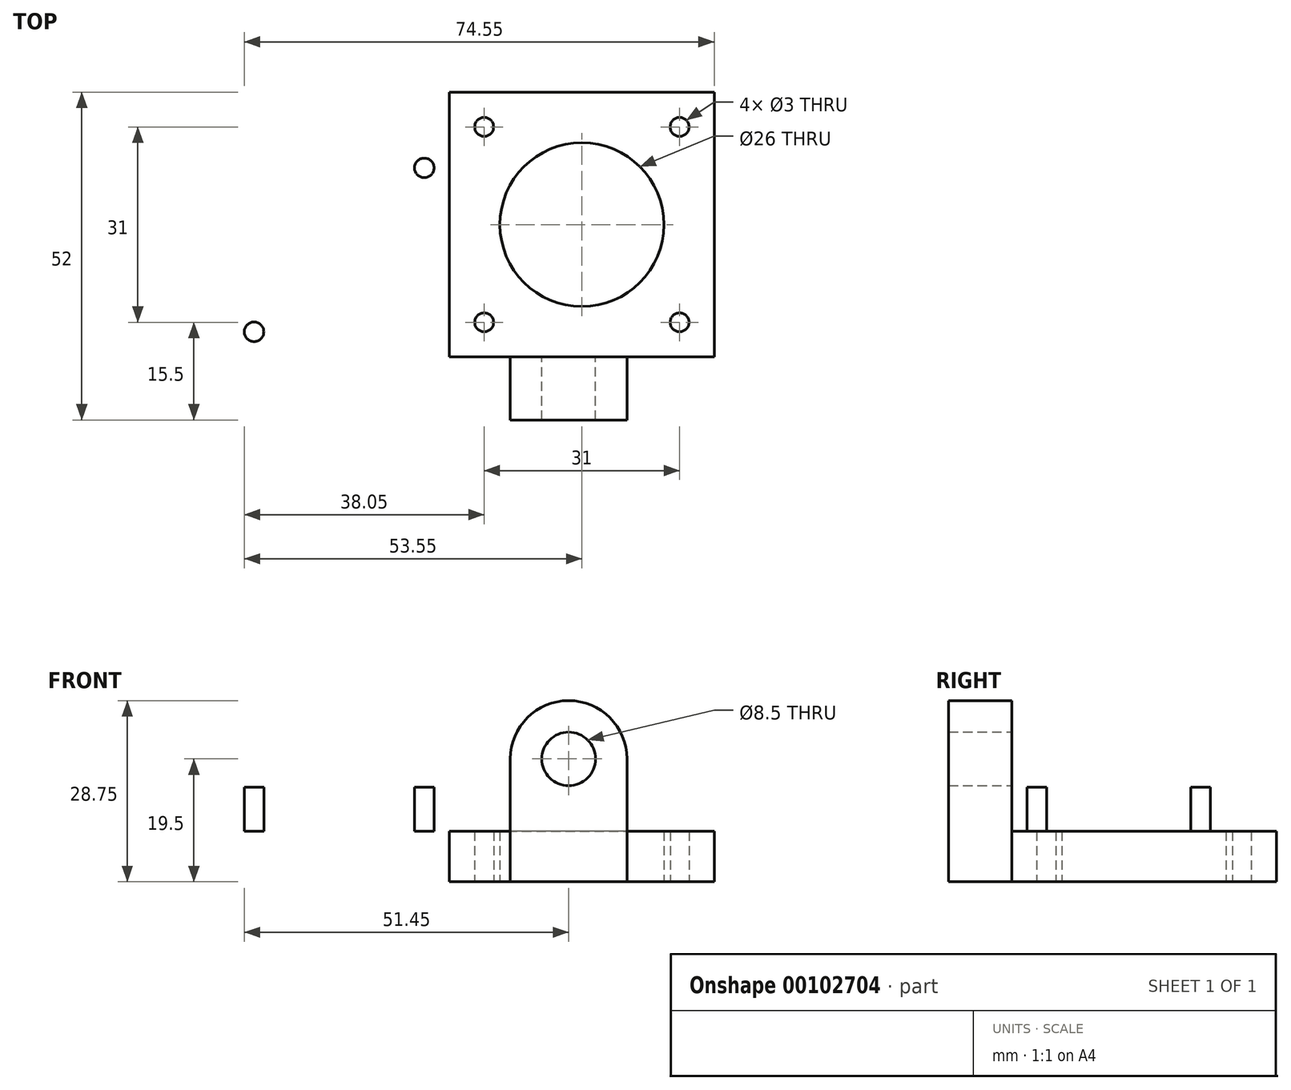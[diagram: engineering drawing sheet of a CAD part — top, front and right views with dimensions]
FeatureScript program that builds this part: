
annotation { "Feature Type Name" : "Feature", "Feature Type Description" : "" }
export const myFeature = defineFeature(function(context is Context, id is Id, definition is map)
    precondition{}
    {
        {
            var Q0;
            Q0=qCreatedBy(makeId("Top.planeOp"),FACE);
            var sketch = newSketch(context, id + "F0", { "sketchPlane" : qUnion([Q0])});
            skLineSegment(sketch, "E0.top", {"start": v(-21, 21) * mm, "end": v(21, 21) * mm});
            skLineSegment(sketch, "E0.left", {"start": v(-21, -21) * mm, "end": v(-21, 21) * mm});
            skPoint(sketch, "E1", {"position": v(0, -21) * mm});
            skCircle(sketch, "E2", {"center": v(-15.5, -15.5) * mm, "radius": 1.5 * mm});
            skCircle(sketch, "E3.MirrorC", {"center": v(15.5, -15.5) * mm, "radius": 1.5 * mm});
            skCircle(sketch, "E4.MirrorC", {"center": v(-15.5, 15.5) * mm, "radius": 1.5 * mm});
            skCircle(sketch, "E5.MirrorC", {"center": v(15.5, 15.5) * mm, "radius": 1.5 * mm});
            skLineSegment(sketch, "E6", {"start": v(-16, -21) * mm, "end": v(-21, -16) * mm, "construction": true});
            skLineSegment(sketch, "E7.MirrorCS", {"start": v(16, -21) * mm, "end": v(21, -16) * mm, "construction": true});
            skLineSegment(sketch, "E8.MirrorCS", {"start": v(-16, 21) * mm, "end": v(-21, 16) * mm, "construction": true});
            skLineSegment(sketch, "E9.MirrorCS", {"start": v(16, 21) * mm, "end": v(21, 16) * mm, "construction": true});
            skCircle(sketch, "E10", {"center": v(0, 0) * mm, "radius": 11 * mm, "construction": true});
            skLineSegment(sketch, "E11", {"start": v(-4, -21) * mm, "end": v(-4, -47.52) * mm, "construction": true});
            skLineSegment(sketch, "E12.MirrorCS", {"start": v(4, -21) * mm, "end": v(4, -47.52) * mm, "construction": true});
            skLineSegment(sketch, "E13", {"start": v(0, -21) * mm, "end": v(21, -21) * mm});
            skCircle(sketch, "E14", {"center": v(0, 0) * mm, "radius": 13 * mm});
            skLineSegment(sketch, "E15", {"start": v(21, -16) * mm, "end": v(21, 21) * mm});
            skLineSegment(sketch, "E16", {"start": v(0, -21) * mm, "end": v(-21, -21) * mm});
            skLineSegment(sketch, "E17", {"start": v(21, -21) * mm, "end": v(21, -16) * mm});
            skPoint(sketch, "E18", {"position": v(-21, 0) * mm});
            skLineSegment(sketch, "E19", {"start": v(-22, -21) * mm, "end": v(-22, 21) * mm, "construction": true});
            skLineSegment(sketch, "E20", {"start": v(-21, -21) * mm, "end": v(-56, -21) * mm});
            skLineSegment(sketch, "E21", {"start": v(-56, -21) * mm, "end": v(-56, 13) * mm});
            skLineSegment(sketch, "E22", {"start": v(-56, 13) * mm, "end": v(-21, 13) * mm});
            skLineSegment(sketch, "E23", {"start": v(-38.5, 13) * mm, "end": v(-38.5, -21) * mm, "construction": true});
            skLineSegment(sketch, "E24", {"start": v(-56, -4) * mm, "end": v(-21, -4) * mm, "construction": true});
            skCircle(sketch, "E25", {"center": v(-52, 9) * mm, "radius": 1.55 * mm});
            skCircle(sketch, "E26.MirrorC", {"center": v(-25, 9) * mm, "radius": 1.55 * mm});
            skCircle(sketch, "E27.MirrorC", {"center": v(-52, -17) * mm, "radius": 1.55 * mm});
            skCircle(sketch, "E28.MirrorC", {"center": v(-25, -17) * mm, "radius": 1.55 * mm});
            skSolve(sketch);
        }
        {
            var Q0;
            Q0 = qSketchRegion(id + "F0", true);
            extrude(context, id + "F1", {"entities" : qUnion([Q0]), "depth" : 8 * mm});
        }
        {
            var Q0;
            Q0=makeQuery(id+"F1.opExtrude","SWEPT_FACE",FACE,{"disambiguationData":[OSD([sQuery(id+"F0.wireOp",EDGE,"E13"),sQuery(id+"F0.wireOp",EDGE,"E16")])]});
            var sketch = newSketch(context, id + "F2", { "sketchPlane" : qUnion([Q0])});
            skCircle(sketch, "E29", {"center": v(-2.1, 19.5) * mm, "radius": 4.25 * mm});
            skLineSegment(sketch, "E30.0", {"start": v(-13, 8) * mm, "end": v(13, 8) * mm});
            skPoint(sketch, "E31", {"position": v(0, 8) * mm});
            skLineSegment(sketch, "E32", {"start": v(-11.35, 19.5) * mm, "end": v(-11.35, 0) * mm});
            skLineSegment(sketch, "E33.MirrorCS", {"start": v(7.15, 19.5) * mm, "end": v(7.15, 0) * mm});
            skArc(sketch, "E34", {"start": v(7.15, 19.5) * mm, "mid": v(-2.1, 28.75) * mm, "end": v(-11.35, 19.5) * mm});
            skLineSegment(sketch, "E35", {"start": v(-2.1, 19.5) * mm, "end": v(-2.1, -7.76) * mm, "construction": true});
            skSolve(sketch);
        }
        {
            var Q0;
            {var subQ0=sQuery(id+"F2.wireOp",EDGE,"E33.MirrorCS");var subQ1=sQuery(id+"F2.wireOp",EDGE,"E30.0");var subQ2=makeQuery(id+"F2.imprint","INTERSECT",VERTEX,{"derivedFrom":[subQ1,subQ0]});Q0=makeQuery(id+"F2.imprint","IMPRINT",FACE,{"disambiguationData":[TD([[makeQuery(id+"F2.imprint","IMPRINT",EDGE,{"disambiguationData":[TD([[subQ2,-1.0]])],"derivedFrom":subQ1}),1.0]])]});}
            var Q1;
            Q1=makeQuery(id+"F2.imprint","IMPRINT",FACE,{"disambiguationData":[TD([[makeQuery(id+"F2.imprint","IMPRINT",EDGE,{"derivedFrom":sQuery(id+"F2.wireOp",EDGE,"E29")}),-1.0]])]});
            var Q2;
            Q2=makeQuery(id+"F1.opExtrude","SWEPT_FACE",FACE,{"disambiguationData":[OSD([sQuery(id+"F0.wireOp",EDGE,"E16")])]});
            extrude(context, id + "F3", {"entities" : qUnion([Q0, Q1]), "operationType" : NewBodyOperationType.ADD, "endBoundEntityFace" : qUnion([Q2]), "depth" : 10 * mm});
        }
        {
            var Q0;
            {var subQ0=sQuery(id+"F0.wireOp",EDGE,"E21");var subQ6=sQuery(id+"F0.wireOp",EDGE,"E20");var subQ8=sQuery(id+"F0.wireOp",EDGE,"E16");var subQ11=sQuery(id+"F0.wireOp",EDGE,"E13");Q0=makeQuery(id+"F3.boolean.opBoolean","SPLIT",FACE,{"disambiguationData":[TD([makeQuery(id+"F1.opExtrude","SWEPT_FACE",FACE,{"disambiguationData":[OSD([subQ0])]})])],"derivedFrom":makeQuery(id+"F1.opExtrude","SWEPT_FACE",FACE,{"disambiguationData":[OSD([subQ11,subQ8,subQ6])]})});}
            var sketch = newSketch(context, id + "F4", { "sketchPlane" : qUnion([Q0])});
            skLineSegment(sketch, "E36", {"start": v(-56, 8) * mm, "end": v(-56, 15) * mm});
            skPoint(sketch, "E37.0", {"position": v(-22, 0) * mm});
            skLineSegment(sketch, "E38", {"start": v(-22, 0) * mm, "end": v(-22, 15) * mm});
            skLineSegment(sketch, "E39", {"start": v(-22, 15) * mm, "end": v(-56, 15) * mm});
            skArc(sketch, "E40", {"start": v(-49.25, 15) * mm, "mid": v(-39, 4.75) * mm, "end": v(-28.75, 15) * mm});
            skLineSegment(sketch, "E41.0", {"start": v(-56, 8) * mm, "end": v(-56, 0) * mm});
            skLineSegment(sketch, "E42.0", {"start": v(-21, 0) * mm, "end": v(-56, 0) * mm});
            skSolve(sketch);
        }
        {
            var Q0;
            {var subQ0=sQuery(id+"F4.wireOp",EDGE,"E36");Q0=makeQuery(id+"F4.imprint","IMPRINT",FACE,{"disambiguationData":[TD([[makeQuery(id+"F4.imprint","IMPRINT",EDGE,{"derivedFrom":subQ0}),-1.0]])]});}
            var Q1;
            {var subQ0=sQuery(id+"F4.wireOp",EDGE,"E39");var subQ1=sQuery(id+"F4.wireOp",EDGE,"E38");var subQ2=makeQuery(id+"F4.imprint","INTERSECT",VERTEX,{"derivedFrom":[subQ1,subQ0]});Q1=makeQuery(id+"F4.imprint","IMPRINT",FACE,{"disambiguationData":[TD([[makeQuery(id+"F4.imprint","IMPRINT",EDGE,{"disambiguationData":[TD([[subQ2,-1.0]])],"derivedFrom":subQ0}),1.0]])]});}
            var Q2;
            Q2=makeQuery(id+"F1.opExtrude","SWEPT_FACE",FACE,{"disambiguationData":[OSD([sQuery(id+"F0.wireOp",EDGE,"E22")])]});
            extrude(context, id + "F5", {"entities" : qUnion([Q0, Q1]), "operationType" : NewBodyOperationType.ADD, "endBound" : BoundingType.UP_TO_SURFACE, "oppositeDirection" : true, "endBoundEntityFace" : qUnion([Q2]), "depth" : 25 * mm});
        }
        {
            var Q0;
            {var subQ0=sQuery(id+"F4.wireOp",EDGE,"E40");var subQ1=sQuery(id+"F2.wireOp",EDGE,"E32");var subQ2=sQuery(id+"F0.wireOp",EDGE,"E20");var subQ3=sQuery(id+"F0.wireOp",EDGE,"E16");var subQ4=sQuery(id+"F0.wireOp",EDGE,"E13");var subQ5=sQuery(id+"F0.wireOp",EDGE,"E21");var subQ6=makeQuery(id+"F3.boolean.opBoolean","SPLIT",EDGE,{"disambiguationData":[TD([makeQuery(id+"F1.opExtrude","CAP_FACE",FACE,{"disambiguationData":[OSD([sQuery(id+"F0.wireOp",EDGE,"E0.top"),sQuery(id+"F0.wireOp",EDGE,"E0.left"),sQuery(id+"F0.wireOp",EDGE,"E2"),sQuery(id+"F0.wireOp",EDGE,"E3.MirrorC"),sQuery(id+"F0.wireOp",EDGE,"E4.MirrorC"),sQuery(id+"F0.wireOp",EDGE,"E5.MirrorC"),subQ4,sQuery(id+"F0.wireOp",EDGE,"E14"),sQuery(id+"F0.wireOp",EDGE,"E15"),subQ3,sQuery(id+"F0.wireOp",EDGE,"E17"),subQ2,subQ5,sQuery(id+"F0.wireOp",EDGE,"E22"),sQuery(id+"F0.wireOp",EDGE,"E25"),sQuery(id+"F0.wireOp",EDGE,"E26.MirrorC"),sQuery(id+"F0.wireOp",EDGE,"E27.MirrorC"),sQuery(id+"F0.wireOp",EDGE,"E28.MirrorC")])],"isStart":false}),makeQuery(id+"F1.opExtrude","SWEPT_FACE",FACE,{"disambiguationData":[OSD([subQ4,subQ3,subQ2])]}),makeQuery(id+"F1.opExtrude","SWEPT_FACE",FACE,{"disambiguationData":[OSD([subQ5])]}),makeQuery(id+"F3.opExtrude","CAP_FACE",FACE,{"disambiguationData":[OSD([subQ4,subQ3,subQ2,sQuery(id+"F2.wireOp",EDGE,"E29"),subQ1,sQuery(id+"F2.wireOp",EDGE,"E33.MirrorCS"),sQuery(id+"F2.wireOp",EDGE,"E34")])],"isStart":true}),makeQuery(id+"F3.opExtrude","SWEPT_FACE",FACE,{"disambiguationData":[OSD([subQ1])]})])],"derivedFrom":makeQuery(id+"F1.opExtrude","CAP_EDGE",EDGE,{"disambiguationData":[OSD([subQ4,subQ3,subQ2])],"isStart":false})});var subQ7=makeQuery(id+"F4.imprint","INTERSECT",VERTEX,{"disambiguationData":[OD(0.0)],"derivedFrom":[subQ6,subQ0]});Q0=makeQuery(id+"F4.imprint","IMPRINT",FACE,{"disambiguationData":[TD([[makeQuery(id+"F4.imprint","IMPRINT",EDGE,{"disambiguationData":[TD([[subQ7,-1.0]])],"derivedFrom":subQ0}),1.0]])]});}
            extrude(context, id + "F6", {"entities" : qUnion([Q0]), "operationType" : NewBodyOperationType.REMOVE, "endBound" : BoundingType.THROUGH_ALL, "oppositeDirection" : true, "depth" : 25 * mm});
        }
        {
            var Q0;
            Q0=makeQuery(id+"F0.imprint","IMPRINT",FACE,{"disambiguationData":[TD([[makeQuery(id+"F0.imprint","IMPRINT",EDGE,{"derivedFrom":sQuery(id+"F0.wireOp",EDGE,"E27.MirrorC")}),-1.0]])]});
            var Q1;
            Q1=makeQuery(id+"F0.imprint","IMPRINT",FACE,{"disambiguationData":[TD([[makeQuery(id+"F0.imprint","IMPRINT",EDGE,{"derivedFrom":sQuery(id+"F0.wireOp",EDGE,"E28.MirrorC")}),1.0]])]});
            var Q2;
            Q2=makeQuery(id+"F0.imprint","IMPRINT",FACE,{"disambiguationData":[TD([[makeQuery(id+"F0.imprint","IMPRINT",EDGE,{"derivedFrom":sQuery(id+"F0.wireOp",EDGE,"E26.MirrorC")}),-1.0]])]});
            var Q3;
            Q3=makeQuery(id+"F0.imprint","IMPRINT",FACE,{"disambiguationData":[TD([[makeQuery(id+"F0.imprint","IMPRINT",EDGE,{"derivedFrom":sQuery(id+"F0.wireOp",EDGE,"E25")}),1.0]])]});
            extrude(context, id + "F7", {"entities" : qUnion([Q0, Q1, Q2, Q3]), "operationType" : NewBodyOperationType.REMOVE, "endBound" : BoundingType.THROUGH_ALL, "depth" : 25 * mm});
        }
    });
